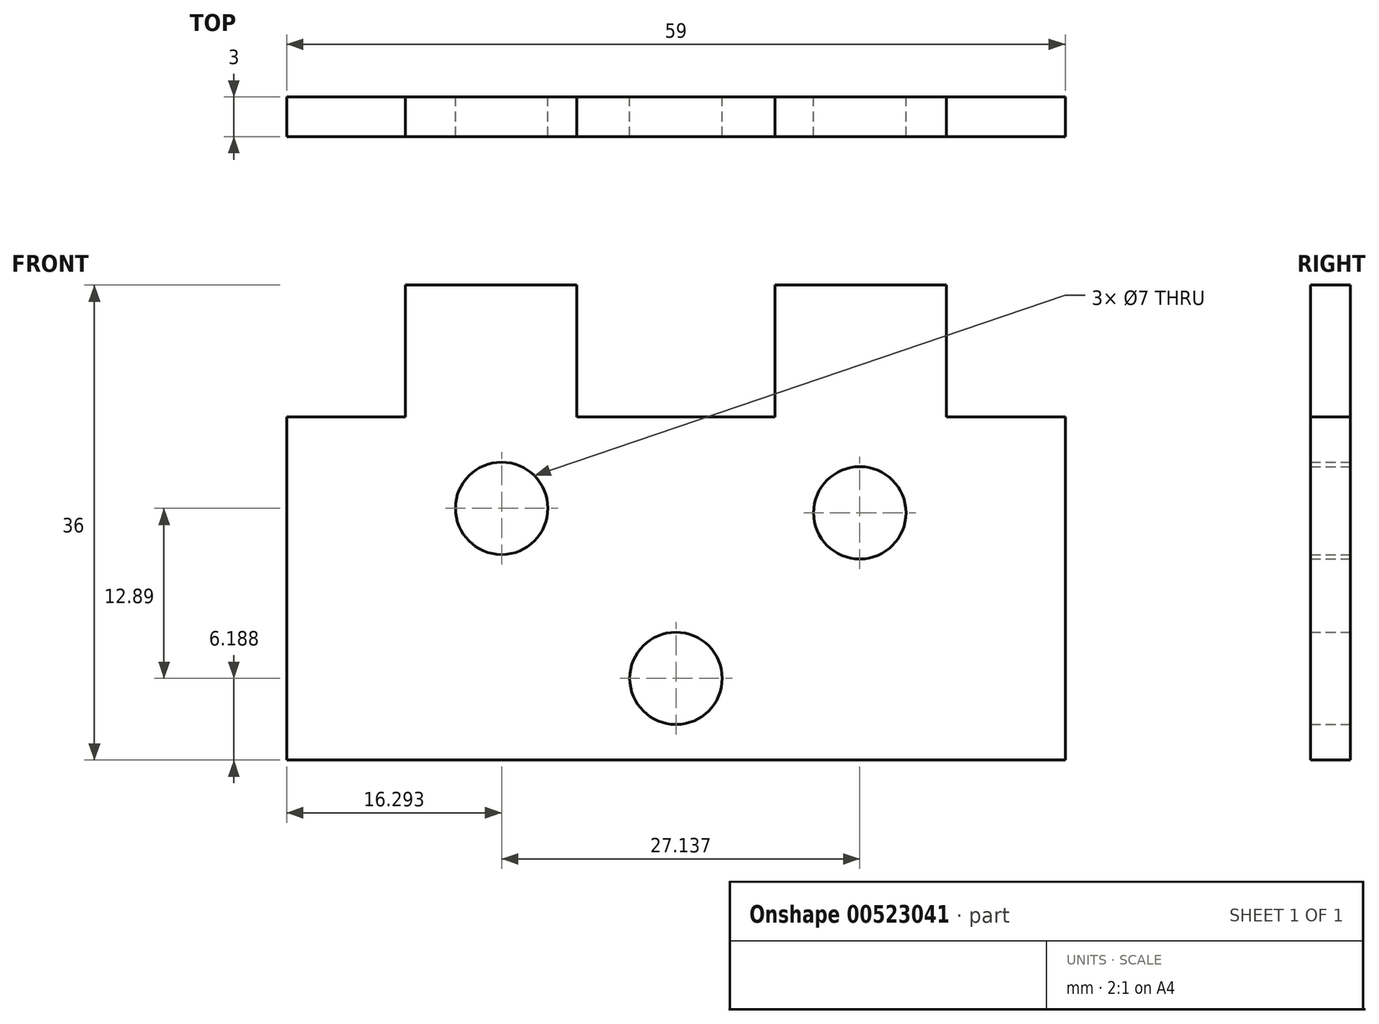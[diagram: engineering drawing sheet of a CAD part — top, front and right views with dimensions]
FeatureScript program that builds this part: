
annotation { "Feature Type Name" : "Feature", "Feature Type Description" : "" }
export const myFeature = defineFeature(function(context is Context, id is Id, definition is map)
    precondition{}
    {
        {
            var Q0;
            Q0=qCreatedBy(makeId("Front.planeOp"),FACE);
            var sketch = newSketch(context, id + "F0", { "sketchPlane" : qUnion([Q0])});
            skLineSegment(sketch, "E0.bottom", {"start": v(29.5, -13) * mm, "end": v(-29.5, -13) * mm});
            skLineSegment(sketch, "E0.top", {"start": v(29.5, 13) * mm, "end": v(-29.5, 13) * mm});
            skLineSegment(sketch, "E0.left", {"start": v(29.5, -13) * mm, "end": v(29.5, 13) * mm});
            skLineSegment(sketch, "E0.right", {"start": v(-29.5, -13) * mm, "end": v(-29.5, 13) * mm});
            skPoint(sketch, "E0.middle", {"position": v(0, 0) * mm});
            skLineSegment(sketch, "E1.bottom", {"start": v(-7.5, 13) * mm, "end": v(-20.5, 13) * mm});
            skLineSegment(sketch, "E1.top", {"start": v(-7.5, 23) * mm, "end": v(-20.5, 23) * mm});
            skLineSegment(sketch, "E1.left", {"start": v(-7.5, 13) * mm, "end": v(-7.5, 23) * mm});
            skLineSegment(sketch, "E1.right", {"start": v(-20.5, 13) * mm, "end": v(-20.5, 23) * mm});
            skPoint(sketch, "E1.middle", {"position": v(-14, 18) * mm});
            skLineSegment(sketch, "E2.bottom", {"start": v(20.5, 13) * mm, "end": v(7.5, 13) * mm});
            skLineSegment(sketch, "E2.top", {"start": v(20.5, 23) * mm, "end": v(7.5, 23) * mm});
            skLineSegment(sketch, "E2.left", {"start": v(20.5, 13) * mm, "end": v(20.5, 23) * mm});
            skLineSegment(sketch, "E2.right", {"start": v(7.5, 13) * mm, "end": v(7.5, 23) * mm});
            skPoint(sketch, "E2.middle", {"position": v(14, 18) * mm});
            skCircle(sketch, "E3", {"center": v(-13.2, 6.08) * mm, "radius": 3.5 * mm});
            skCircle(sketch, "E4", {"center": v(13.93, 5.74) * mm, "radius": 3.5 * mm});
            skCircle(sketch, "E5", {"center": v(0, -6.81) * mm, "radius": 3.5 * mm});
            skSolve(sketch);
        }
        {
            var Q0;
            Q0 = qSketchRegion(id + "F0", true);
            extrude(context, id + "F1", {"entities" : qUnion([Q0]), "endBound" : BoundingType.SYMMETRIC, "depth" : 3 * mm, "offsetDistance" : 25 * mm});
        }
    });
